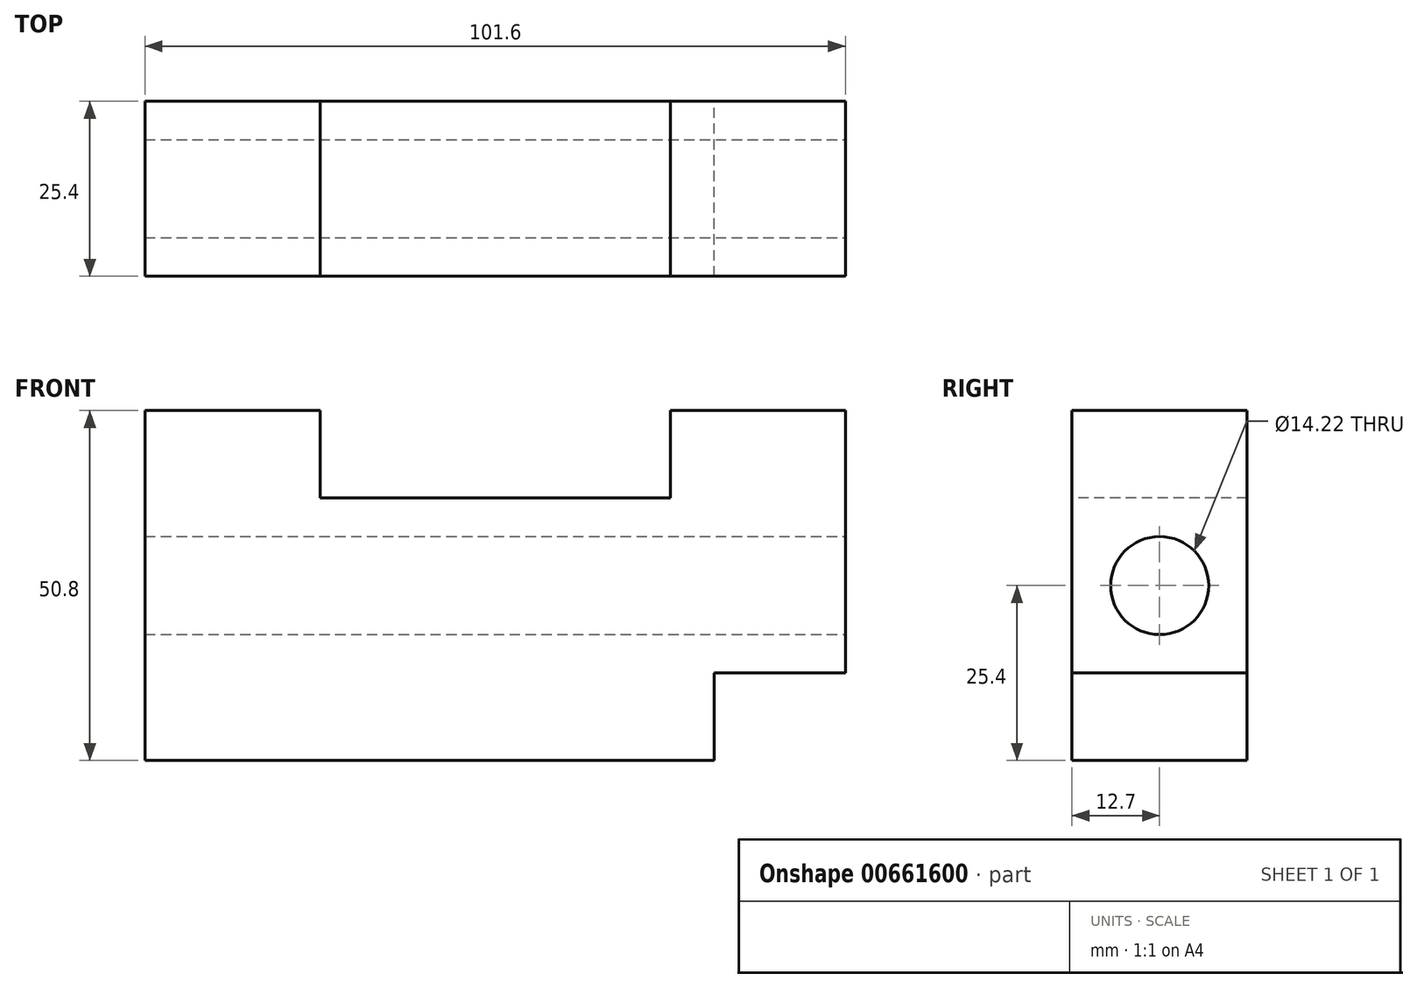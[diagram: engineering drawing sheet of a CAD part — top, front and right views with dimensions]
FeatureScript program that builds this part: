
annotation { "Feature Type Name" : "Feature", "Feature Type Description" : "" }
export const myFeature = defineFeature(function(context is Context, id is Id, definition is map)
    precondition{}
    {
        {
            var Q0;
            Q0=qCreatedBy(makeId("Front.planeOp"),FACE);
            var sketch = newSketch(context, id + "F0", { "sketchPlane" : qUnion([Q0])});
            skLineSegment(sketch, "E0.bottom", {"start": v(-50.8, 25.4) * mm, "end": v(50.8, 25.4) * mm});
            skLineSegment(sketch, "E0.top", {"start": v(-50.8, -25.4) * mm, "end": v(50.8, -25.4) * mm});
            skLineSegment(sketch, "E0.left", {"start": v(-50.8, 25.4) * mm, "end": v(-50.8, -25.4) * mm});
            skLineSegment(sketch, "E0.right", {"start": v(50.8, 25.4) * mm, "end": v(50.8, -25.4) * mm});
            skPoint(sketch, "E0.middle", {"position": v(0, 0) * mm});
            skSolve(sketch);
        }
        {
            var Q0;
            Q0 = qSketchRegion(id + "F0", true);
            extrude(context, id + "F1", {"entities" : qUnion([Q0]), "depth" : 25.4 * mm, "offsetDistance" : 25.4 * mm});
        }
        {
            var Q0;
            Q0=makeQuery(id+"F1.opExtrude","CAP_FACE",FACE,{"disambiguationData":[OSD([sQuery(id+"F0.wireOp",EDGE,"E0.bottom"),sQuery(id+"F0.wireOp",EDGE,"E0.top"),sQuery(id+"F0.wireOp",EDGE,"E0.left"),sQuery(id+"F0.wireOp",EDGE,"E0.right")])],"isStart":false});
            var sketch = newSketch(context, id + "F2", { "sketchPlane" : qUnion([Q0])});
            skLineSegment(sketch, "E1.bottom", {"start": v(-25.4, 25.4) * mm, "end": v(25.4, 25.4) * mm});
            skLineSegment(sketch, "E1.top", {"start": v(-25.4, 12.7) * mm, "end": v(25.4, 12.7) * mm});
            skLineSegment(sketch, "E1.left", {"start": v(-25.4, 25.4) * mm, "end": v(-25.4, 12.7) * mm});
            skLineSegment(sketch, "E1.right", {"start": v(25.4, 25.4) * mm, "end": v(25.4, 12.7) * mm});
            skSolve(sketch);
        }
        {
            var Q0;
            Q0 = qSketchRegion(id + "F2", true);
            extrude(context, id + "F3", {"entities" : qUnion([Q0]), "operationType" : NewBodyOperationType.REMOVE, "endBound" : BoundingType.THROUGH_ALL, "oppositeDirection" : true, "depth" : 25.4 * mm, "offsetDistance" : 25.4 * mm});
        }
        {
            var Q0;
            Q0=makeQuery(id+"F1.opExtrude","SWEPT_FACE",FACE,{"disambiguationData":[OSD([sQuery(id+"F0.wireOp",EDGE,"E0.right")])]});
            var sketch = newSketch(context, id + "F4", { "sketchPlane" : qUnion([Q0])});
            skLineSegment(sketch, "E2.bottom", {"start": v(-25.4, -25.4) * mm, "end": v(0, -25.4) * mm});
            skLineSegment(sketch, "E2.top", {"start": v(-25.4, -12.7) * mm, "end": v(0, -12.7) * mm});
            skLineSegment(sketch, "E2.left", {"start": v(-25.4, -25.4) * mm, "end": v(-25.4, -12.7) * mm});
            skLineSegment(sketch, "E2.right", {"start": v(0, -25.4) * mm, "end": v(0, -12.7) * mm});
            skSolve(sketch);
        }
        {
            var Q0;
            Q0 = qSketchRegion(id + "F4", true);
            extrude(context, id + "F5", {"entities" : qUnion([Q0]), "operationType" : NewBodyOperationType.REMOVE, "oppositeDirection" : true, "depth" : 19.05 * mm, "offsetDistance" : 25.4 * mm});
        }
        {
            var Q0;
            Q0=makeQuery(id+"F1.opExtrude","SWEPT_FACE",FACE,{"disambiguationData":[OSD([sQuery(id+"F0.wireOp",EDGE,"E0.right")])]});
            var sketch = newSketch(context, id + "F6", { "sketchPlane" : qUnion([Q0])});
            skCircle(sketch, "E3", {"center": v(-12.7, 0) * mm, "radius": 7.11 * mm});
            skSolve(sketch);
        }
        {
            var Q0;
            Q0 = qSketchRegion(id + "F6", true);
            extrude(context, id + "F7", {"entities" : qUnion([Q0]), "operationType" : NewBodyOperationType.REMOVE, "endBound" : BoundingType.THROUGH_ALL, "oppositeDirection" : true, "depth" : 25.4 * mm, "offsetDistance" : 25.4 * mm});
        }
    });
